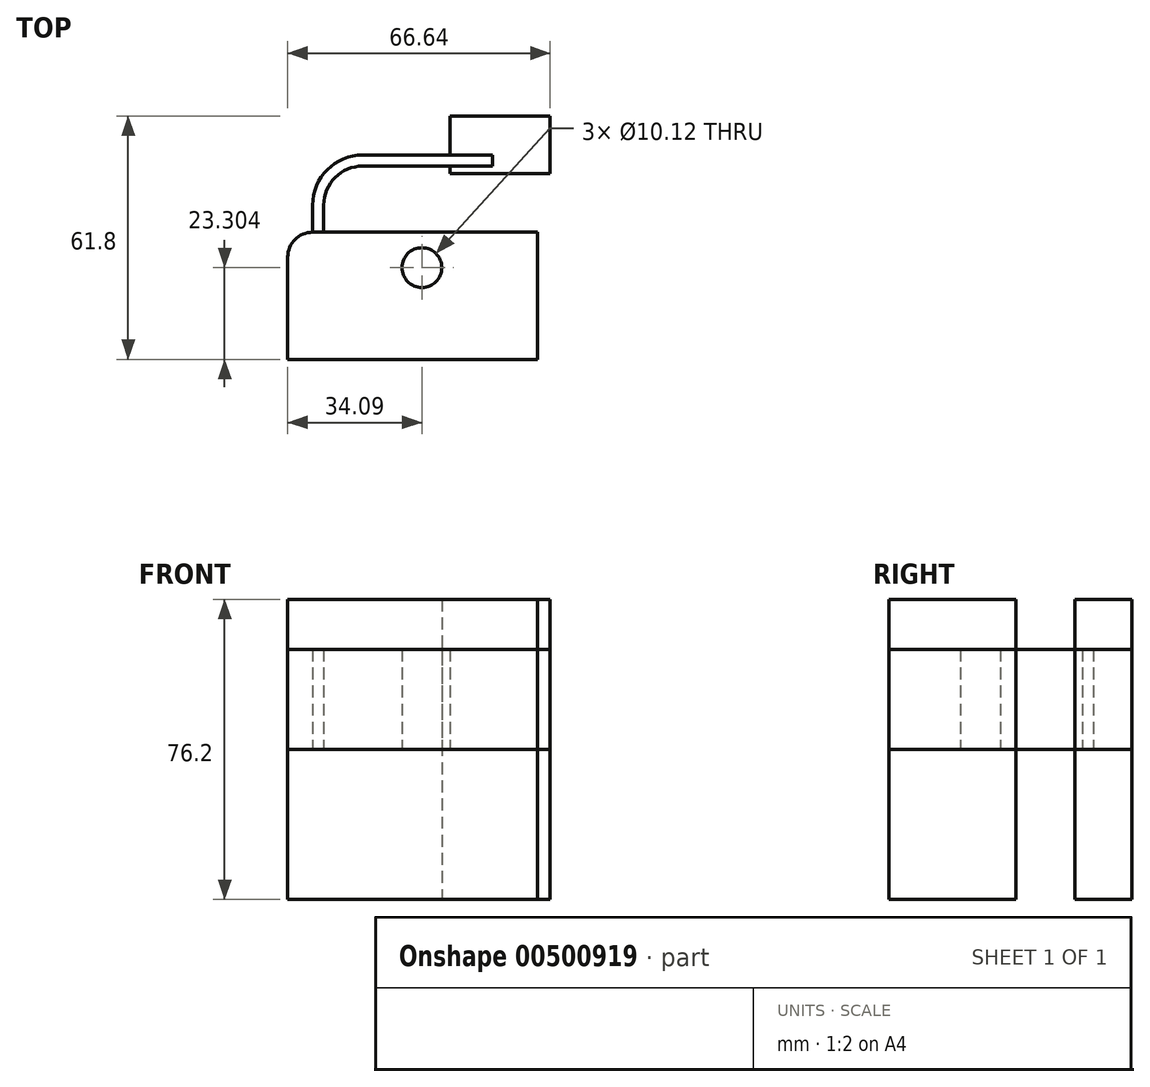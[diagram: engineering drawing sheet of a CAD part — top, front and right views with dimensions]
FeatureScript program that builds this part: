
annotation { "Feature Type Name" : "Feature", "Feature Type Description" : "" }
export const myFeature = defineFeature(function(context is Context, id is Id, definition is map)
    precondition{}
    {
        {
            var Q0;
            Q0=qCreatedBy(makeId("Top.planeOp"),FACE);
            var sketch = newSketch(context, id + "F0", { "sketchPlane" : qUnion([Q0])});
            skLineSegment(sketch, "E0.bottom", {"start": v(-12.7, 15.53) * mm, "end": v(44.45, 15.53) * mm});
            skLineSegment(sketch, "E0.top", {"start": v(-19.05, -16.77) * mm, "end": v(44.45, -16.77) * mm});
            skLineSegment(sketch, "E0.left", {"start": v(-19.05, 9.18) * mm, "end": v(-19.05, -16.77) * mm});
            skLineSegment(sketch, "E0.right", {"start": v(44.45, 15.53) * mm, "end": v(44.45, -16.77) * mm});
            skLineSegment(sketch, "E1.bottom", {"start": v(22.2, 45.03) * mm, "end": v(47.6, 45.03) * mm});
            skLineSegment(sketch, "E1.top", {"start": v(22.2, 30.48) * mm, "end": v(47.6, 30.48) * mm});
            skLineSegment(sketch, "E1.left", {"start": v(22.2, 45.03) * mm, "end": v(22.2, 30.48) * mm});
            skLineSegment(sketch, "E1.right", {"start": v(47.6, 45.03) * mm, "end": v(47.6, 30.48) * mm});
            skArc(sketch, "E2.filletArc", {"start": v(-12.7, 15.53) * mm, "mid": v(-17.2, 13.67) * mm, "end": v(-19.05, 9.18) * mm});
            skLineSegment(sketch, "E3", {"start": v(-12.7, 15.53) * mm, "end": v(-12.7, 22.44) * mm});
            skArc(sketch, "E4", {"start": v(-12.7, 22.44) * mm, "mid": v(-8.98, 31.42) * mm, "end": v(0, 35.14) * mm});
            skLineSegment(sketch, "E5", {"start": v(0, 35.14) * mm, "end": v(33.02, 35.14) * mm});
            skLineSegment(sketch, "E6.0", {"start": v(0, 32.34) * mm, "end": v(33.02, 32.34) * mm});
            skArc(sketch, "E6.1", {"start": v(-9.9, 22.44) * mm, "mid": v(-7, 29.44) * mm, "end": v(0, 32.34) * mm});
            skLineSegment(sketch, "E6.2", {"start": v(-9.9, 15.53) * mm, "end": v(-9.9, 22.44) * mm});
            skLineSegment(sketch, "E7", {"start": v(33.02, 35.14) * mm, "end": v(33.02, 32.34) * mm});
            skCircle(sketch, "E8", {"center": v(15.04, 6.53) * mm, "radius": 5.06 * mm});
            skSolve(sketch);
        }
        {
            var Q0;
            Q0=makeQuery(id+"F0.imprint","IMPRINT",FACE,{"disambiguationData":[TD([[makeQuery(id+"F0.imprint","IMPRINT",EDGE,{"derivedFrom":sQuery(id+"F0.wireOp",EDGE,"E0.bottom")}),-1.0]])]});
            var Q1;
            {var subQ5=sQuery(id+"F0.wireOp",EDGE,"E1.bottom");Q1=makeQuery(id+"F0.imprint","IMPRINT",FACE,{"disambiguationData":[TD([[makeQuery(id+"F0.imprint","IMPRINT",EDGE,{"derivedFrom":subQ5}),-1.0]])]});}
            extrude(context, id + "F1", {"entities" : qUnion([Q0, Q1]), "depth" : 76.2 * mm, "symmetric" : true});
        }
        {
            var Q0;
            Q0 = qSketchRegion(id + "F0", true);
            extrude(context, id + "F2", {"entities" : qUnion([Q0]), "depth" : 25.4 * mm});
        }
        {
            var Q0;
            Q0 = qSketchRegion(id + "F0", true);
            extrude(context, id + "F3", {"entities" : qUnion([Q0]), "depth" : 25.4 * mm});
        }
    });
